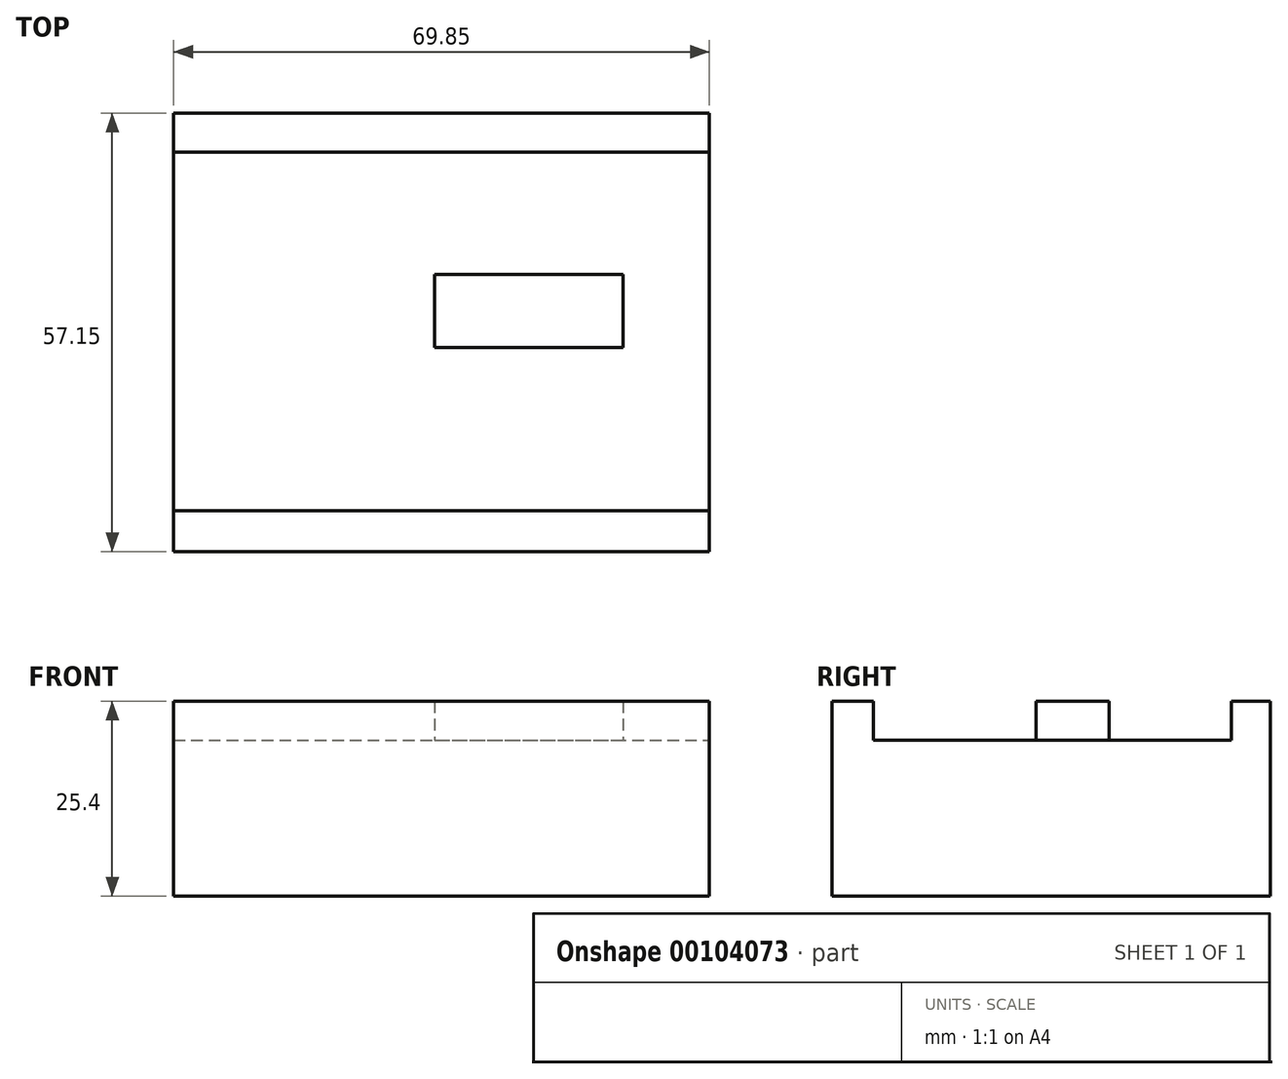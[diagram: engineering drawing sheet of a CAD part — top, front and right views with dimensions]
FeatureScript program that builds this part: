
annotation { "Feature Type Name" : "Feature", "Feature Type Description" : "" }
export const myFeature = defineFeature(function(context is Context, id is Id, definition is map)
    precondition{}
    {
        {
            var Q0;
            Q0=qCreatedBy(makeId("Top.planeOp"),FACE);
            var sketch = newSketch(context, id + "F0", { "sketchPlane" : qUnion([Q0])});
            skLineSegment(sketch, "E0.bottom", {"start": v(-65.32, 36.94) * mm, "end": v(4.53, 36.94) * mm});
            skLineSegment(sketch, "E0.top", {"start": v(-65.32, -20.21) * mm, "end": v(4.53, -20.21) * mm});
            skLineSegment(sketch, "E0.left", {"start": v(-65.32, 36.94) * mm, "end": v(-65.32, -20.21) * mm});
            skLineSegment(sketch, "E0.right", {"start": v(4.53, 36.94) * mm, "end": v(4.53, -20.21) * mm});
            skLineSegment(sketch, "E1", {"start": v(-65.32, 31.87) * mm, "end": v(4.53, 31.87) * mm});
            skLineSegment(sketch, "E2", {"start": v(-65.32, -14.85) * mm, "end": v(4.53, -14.85) * mm});
            skLineSegment(sketch, "E3.bottom", {"start": v(-31.33, 15.9) * mm, "end": v(-6.76, 15.9) * mm});
            skLineSegment(sketch, "E3.top", {"start": v(-31.33, 6.4) * mm, "end": v(-6.76, 6.4) * mm});
            skLineSegment(sketch, "E3.left", {"start": v(-31.33, 15.9) * mm, "end": v(-31.33, 6.4) * mm});
            skLineSegment(sketch, "E3.right", {"start": v(-6.76, 15.9) * mm, "end": v(-6.76, 6.4) * mm});
            skCircle(sketch, "E4", {"center": v(-56.65, -5.06) * mm, "radius": 3.02 * mm});
            skCircle(sketch, "E5", {"center": v(-50.47, -5.06) * mm, "radius": 3.16 * mm});
            skSolve(sketch);
        }
        {
            var Q0;
            {var subQ1=sQuery(id+"F0.wireOp",EDGE,"E1");Q0=makeQuery(id+"F0.imprint","IMPRINT",FACE,{"disambiguationData":[TD([[makeQuery(id+"F0.imprint","IMPRINT",EDGE,{"derivedFrom":subQ1}),-1.0]])]});}
            var Q1;
            Q1=makeQuery(id+"F0.imprint","IMPRINT",FACE,{"disambiguationData":[TD([[makeQuery(id+"F0.imprint","IMPRINT",EDGE,{"derivedFrom":sQuery(id+"F0.wireOp",EDGE,"E4")}),1.0]])]});
            var Q2;
            Q2=makeQuery(id+"F0.imprint","IMPRINT",FACE,{"disambiguationData":[TD([[makeQuery(id+"F0.imprint","IMPRINT",EDGE,{"derivedFrom":sQuery(id+"F0.wireOp",EDGE,"E5")}),1.0]])]});
            extrude(context, id + "F1", {"entities" : qUnion([Q0, Q1, Q2]), "depth" : 20.32 * mm});
        }
        {
            var Q0;
            Q0=makeQuery(id+"F0.imprint","IMPRINT",FACE,{"disambiguationData":[TD([[makeQuery(id+"F0.imprint","IMPRINT",EDGE,{"derivedFrom":sQuery(id+"F0.wireOp",EDGE,"E3.bottom")}),-1.0]])]});
            var Q1;
            {var subQ0=sQuery(id+"F0.wireOp",EDGE,"E0.top");Q1=makeQuery(id+"F0.imprint","IMPRINT",FACE,{"disambiguationData":[TD([[makeQuery(id+"F0.imprint","IMPRINT",EDGE,{"derivedFrom":subQ0}),1.0]])]});}
            var Q2;
            {var subQ0=sQuery(id+"F0.wireOp",EDGE,"E0.bottom");Q2=makeQuery(id+"F0.imprint","IMPRINT",FACE,{"disambiguationData":[TD([[makeQuery(id+"F0.imprint","IMPRINT",EDGE,{"derivedFrom":subQ0}),-1.0]])]});}
            extrude(context, id + "F2", {"entities" : qUnion([Q0, Q1, Q2]), "operationType" : NewBodyOperationType.ADD, "depth" : 25.4 * mm});
        }
    });
